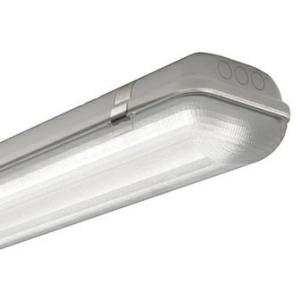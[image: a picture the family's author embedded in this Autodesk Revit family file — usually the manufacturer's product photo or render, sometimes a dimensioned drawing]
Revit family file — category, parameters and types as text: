
# Revit family: 3f_filippi_-_3f_linda_hq_3f_filippi_-_58870_-_3f_linda_led_2x24w-940_l1270
name_source: partatom
category: Lighting Fixtures
units: mm (PartAtom-declared; Revit-internal decimal feet)

## family parameters
Cut with Voids When Loaded = No
Host = Face
Light Source = No
Part Type = Normal
Room Calculation Point = No
Round Connector Dimension = Use Diameter
Shared = No

## types (1)
- 3F Filippi - 3F Linda HQ (1 x LED, 6131 lm, 54.5 W, 4000 K)
    Apparent Load = 55 VA
    Approval mark = CE
    CIE Flux Codes = 46 76 93 97 100
    Color Rendering = 90
    Color Temperature = 4000 K
    Control Gear = Electronic ballast
    Default Elevation = 1800 mm
    Description = ILLUMINOTECHNICAL
Luminous efficiency 100% (DLOR 97%, ULOR 3%).
Initial luminous flux of the luminaire 6131 lm.
Controlled symmetric distribution.
Installation Interdistance Transv.D = 1.52 x hu - Long.D = 1.17 x hu.
Tabular UGR (CIE 117 - 4H-8H; S=0.25H; 70/50/20): RUG 23.5 - 22.6.
Beam angle: 94° - 78°.
Luminous efficacy 112 lm/W.
Lifetime (L93/B10): 30000 h. (tq+25°C)
Lifetime (L90/B10): 50000 h. (tq+25°C)
Lifetime (L85/B10): 80000 h. (tq+25°C)
Lifetime (L80/B10): 100000 h. (tq+25°C)
Lifetime (L85/B10): 50000 h. (tq+35°C)
Sudden decreased luminous flux after 50000 hours: 0% (C0).
Photobiological safety in compliance with IEC/TR 62778: RG0 risk exempt, (IEC 62471).
In compliance with IEC/EN 62722-2-1 - IEC/EN 62717 standards.

SOURCE
2 linear LED modules 24W/940.
Energy efficiency class (UE 2019/2020 - UE 2019/2015): E.
CIE 13.3 Colour rendering index: CRI >90 (R9 >50%).
IES TM-30 Fidelity Index: Rf = 92 Rg = 101.
CCT nominal colour temperature 4000 K.
Colour initial tolerance (MacAdam): SDCM 3.

MECHANICAL
Self-extinguishing V2 polycarbonate housing, injection moulded, RAL 7035 grey.
Ecologic anti-aging injected sealing gasket.
Diffuser in self-extinguishing V2 polycarbonate, photo-engraved interior, UV stabilised, injection moulded with smooth outer surface, tamper-proof opening.
Gear-holder reflector in hot-dip galvanised steel, painted with white polyester base.
Snug fit safety snap-lock clips for diffuser mounting in stainless steel, screwdriver opening.
Fixing brackets in stainless steel.
Possibility for technicians to access the interior of the luminaire.
Luminaire with limited surface temperature. - D - (EN 60598-2-24)
Dimensions: 1270x160 mm, height 100 mm. Weight 2.699 kg.
IP66 protection degree.
Mechanical strength to impacts IK10 (20 joule).
Glow-wire test resistance 850°C.

ELECTRICAL
Halogen Free electronic wiring 230V-50/60Hz, power factor 0.97, THD <25%, constant output current, SELV, class I, 1 driver.
Power of the luminaire 54.5 W.
ENEC - CE.
SAFE FLICKER: PstLM=<1 and SVM=<0.4 (IEC TR 61547-1 and IEC TR 63158), to ensure a more comfortable and safe light.
Luminaire compliant with EN 60598-2-22 for power supply from a centralised emergency system CPSS (Central Power Supply System), not incorporated in the luminaire - high risk areas excluded. The default power and flux are 100% in AC and 100% in DC.
Ambient temperature from -20°C to +35°C.
Temperature class T6 max 85°C.
Relative humidity UR: <85%.

INSTALLATION
Ceiling / Suspended / Wall.
All accessories dedicated to this product are available on the Catalog and on our website www.3F-Filippi.com.

APPLICATIONS
Suitable product for food production plants (HACCP), IFS (Food Version 6), BRC (GSFS Food Version 7).
Dry, dusty indoor environments, subject to occasional water splashes.
Virtually shatterproof polycarbonate compatibly with the fumes / atmospheres that compromise the elasticity of plastic materials.
Not suitable for installation on surfaces subject to important vibrations, exposed to weather conditions, on ropes or poles.
Suitable for illumination of public car parks and parking grounds referred to DIN 67528:2018-04.

WARNING
Fixture not suitable for cold stores with an ambient temperature <0°C and/or relative humidity >85%.
Luminaire designed for disposal/recycling at end-of-life.
Replaceable (LED only) light source by a professional. Replaceable control gear by a professional.
    Height = 100 mm  [stored 0.328084 ft]
    Lamp = 1 x LED
    Lamp Light Flux = 6131 lm
    Lamp Power = 54.5 W
    Lamp count = 1
    Length = 1270 mm
    Lifetime = 50000 h
    Luminous efficacy = 113 lm/W
    Manufacturer = 3F Filippi
    ModVariant = No
    Model = 3F Filippi - 58870 - 3F Linda LED 2x24W-940 L1270
    Mounting Place = Ceiling
    Mounting Type = Pendant
    Number of Poles = 1
    OnlyDefault = Yes
    Power Factor = 1
    Product Name = 3F Filippi - 3F Linda HQ
    Product group = pendant luminaire
    ProductGroupID = 9
    Protection Class = Protection class I
    Protection Degree = IP 66
    RLX_Detail_Level = 1
    RLX_Emergency_Light_Flux = 0 lm
    RLX_Emergency_Type = 0
    RLX_Emergency_Type_DB = No
    RlxData = <blob elided: 71665 chars, md5=c56c2a62>
    Socket = socket
    Standby Power = 0 W
    System Light Flux = 6131 lm
    System Power = 55 W
    Type Comments = Product without accessories
    Type Image = 3ffilippi_3f_linda_led_2x.jpg
    URL = http://relux.com
    VarID = ---
    Voltage = 0 V
    Weight = 0.00 kg
    Width = 160 mm

note: [stored X ft] marks values corroborated as IEEE doubles in the binary element streams (Revit-internal decimal feet)

## geometry (parser evidence)
native form markers: Blend x4, Sweep x9
no freeform markers — native parametric forms only
